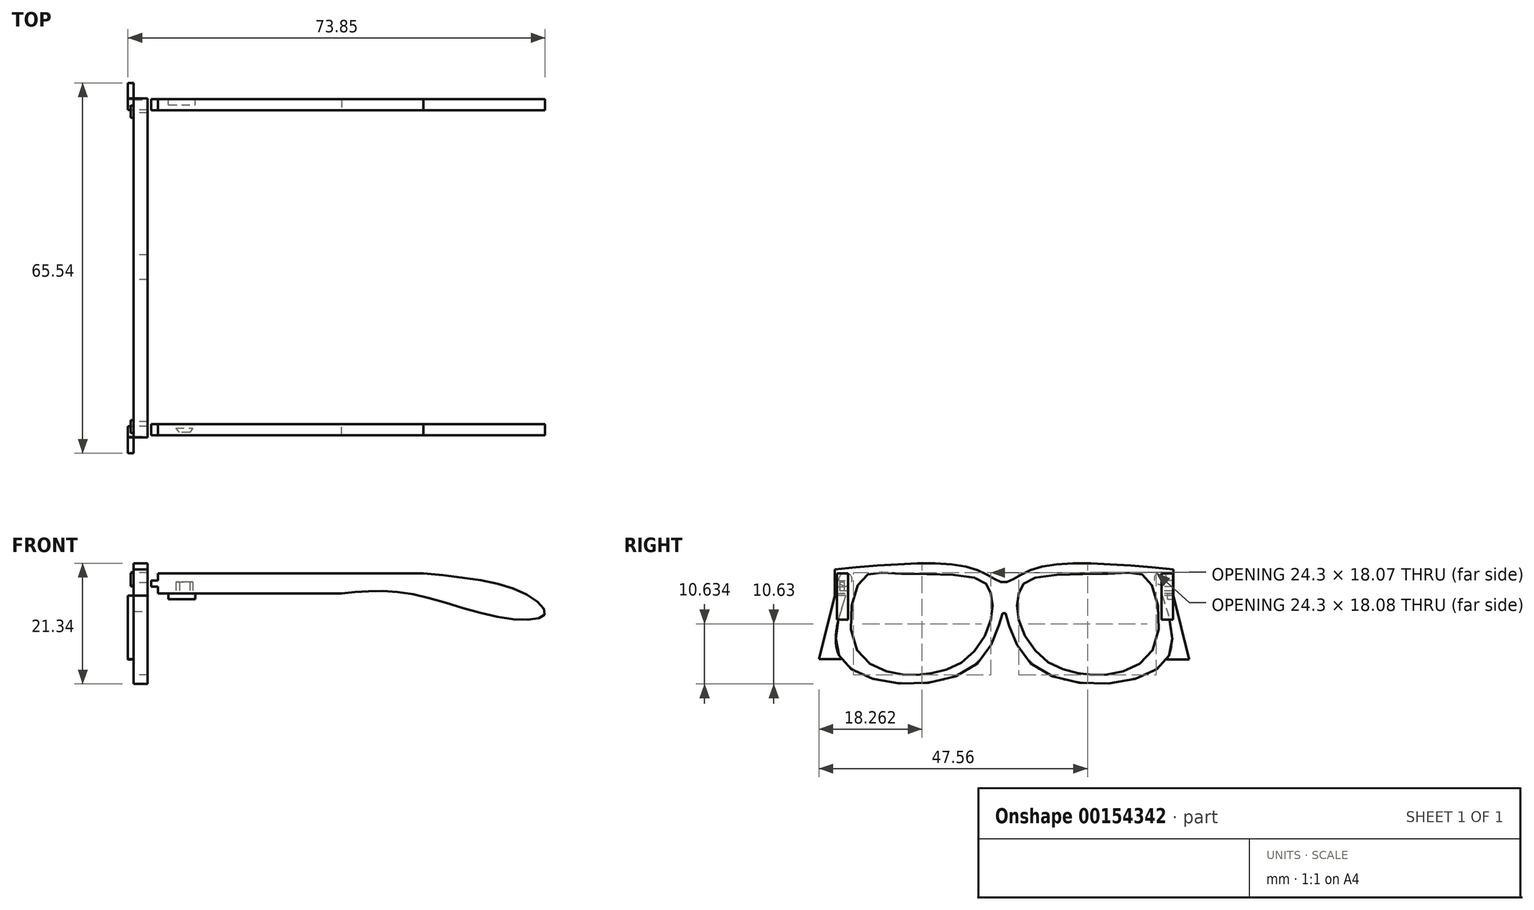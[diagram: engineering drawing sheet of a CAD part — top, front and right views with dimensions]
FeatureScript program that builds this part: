
annotation { "Feature Type Name" : "Feature", "Feature Type Description" : "" }
export const myFeature = defineFeature(function(context is Context, id is Id, definition is map)
    precondition{}
    {
        {
            var Q0;
            Q0=qCreatedBy(makeId("Front.planeOp"),FACE);
            var sketch = newSketch(context, id + "F0", { "sketchPlane" : qUnion([Q0])});
            skLineSegment(sketch, "E0", {"start": v(-30.17, 0) * mm, "end": v(-30.17, 1.2) * mm});
            skLineSegment(sketch, "E1", {"start": v(-30.17, 1.2) * mm, "end": v(-31.35, 1.2) * mm});
            skLineSegment(sketch, "E2", {"start": v(-31.35, 1.2) * mm, "end": v(-31.35, 2.3) * mm});
            skLineSegment(sketch, "E3", {"start": v(-31.35, 2.3) * mm, "end": v(-30.17, 2.3) * mm});
            skLineSegment(sketch, "E4", {"start": v(-30.17, 2.3) * mm, "end": v(-30.17, 3.57) * mm});
            skLineSegment(sketch, "E5", {"start": v(-30.17, 3.57) * mm, "end": v(16.84, 3.57) * mm});
            skLineSegment(sketch, "E6", {"start": v(-30.17, 0) * mm, "end": v(2.32, 0) * mm});
            skFitSpline(sketch, "E7", {"points": [v(16.84, 3.57) * mm, v(34.72, 0) * mm, v(38.32, -3.7) * mm, v(31, -4.33) * mm, v(14.06, 0) * mm, v(2.32, 0) * mm], "startDerivative": vector(80.04, -8.07) * mm, "endDerivative": vector(-54.78, -5.44) * mm});
            skSolve(sketch);
        }
        {
            var Q0;
            Q0=makeQuery(id+"F0.imprint","IMPRINT",FACE,{"disambiguationData":[TD([[makeQuery(id+"F0.imprint","IMPRINT",EDGE,{"derivedFrom":sQuery(id+"F0.wireOp",EDGE,"E0")}),-1.0]])]});
            extrude(context, id + "F1", {"entities" : qUnion([Q0]), "endBound" : BoundingType.SYMMETRIC, "depth" : 2 * mm});
        }
        {
            var Q0;
            Q0=makeQuery(id+"F1.opExtrude","SWEPT_BODY",BODY,{"disambiguationData":[OSD([sQuery(id+"F0.wireOp",EDGE,"E0"),sQuery(id+"F0.wireOp",EDGE,"E1"),sQuery(id+"F0.wireOp",EDGE,"E2"),sQuery(id+"F0.wireOp",EDGE,"E3"),sQuery(id+"F0.wireOp",EDGE,"E4"),sQuery(id+"F0.wireOp",EDGE,"E5"),sQuery(id+"F0.wireOp",EDGE,"E6"),sQuery(id+"F0.wireOp",EDGE,"E7")])]});
            var Q1;
            Q1=makeQuery(id+"F1.opExtrude","CAP_FACE",FACE,{"disambiguationData":[OSD([sQuery(id+"F0.wireOp",EDGE,"E0"),sQuery(id+"F0.wireOp",EDGE,"E1"),sQuery(id+"F0.wireOp",EDGE,"E2"),sQuery(id+"F0.wireOp",EDGE,"E3"),sQuery(id+"F0.wireOp",EDGE,"E4"),sQuery(id+"F0.wireOp",EDGE,"E5"),sQuery(id+"F0.wireOp",EDGE,"E6"),sQuery(id+"F0.wireOp",EDGE,"E7")])],"isStart":false});
            mirror(context, id + "F2", {"entities" : qUnion([Q0]), "mirrorPlane" : qUnion([Q1])});
        }
        {
            var Q0;
            Q0=makeQuery(id+"F2.opPattern","COPY",BODY,{"derivedFrom":makeQuery(id+"F1.opExtrude","SWEPT_BODY",BODY,{"disambiguationData":[OSD([sQuery(id+"F0.wireOp",EDGE,"E0"),sQuery(id+"F0.wireOp",EDGE,"E1"),sQuery(id+"F0.wireOp",EDGE,"E2"),sQuery(id+"F0.wireOp",EDGE,"E3"),sQuery(id+"F0.wireOp",EDGE,"E4"),sQuery(id+"F0.wireOp",EDGE,"E5"),sQuery(id+"F0.wireOp",EDGE,"E6"),sQuery(id+"F0.wireOp",EDGE,"E7")])]}),"instanceName":"1"});
            transform(context, id + "F3", {"entities" : qUnion([Q0]), "transformType" : TransformType.TRANSLATION_3D, "dx" : 0 * mm, "dy" : 50.13 * mm, "dz" : 0 * mm, "makeCopy" : false});
        }
        {
            var Q0;
            Q0=qCreatedBy(makeId("Right.planeOp"),FACE);
            var sketch = newSketch(context, id + "F4", { "sketchPlane" : qUnion([Q0])});
            skLineSegment(sketch, "E8", {"start": v(53.4, 28.28) * mm, "end": v(53.4, 23.62) * mm});
            skLineSegment(sketch, "E9", {"start": v(-6.6, 23.62) * mm, "end": v(-6.6, 28.28) * mm});
            skPoint(sketch, "E10", {"position": v(28.4, 28.28) * mm});
            skPoint(sketch, "E11", {"position": v(18.4, 28.28) * mm});
            skPoint(sketch, "E12.2.internal.snap0", {"position": v(53.4, 25.95) * mm});
            skFitSpline(sketch, "E12", {"points": [v(53.4, 28.28) * mm, v(28.4, 28.28) * mm, v(23.4, 25.95) * mm, v(18.4, 28.28) * mm, v(-6.6, 28.28) * mm], "startDerivative": vector(-87.84, 8.09) * mm, "endDerivative": vector(-87.84, -8.09) * mm});
            skPoint(sketch, "E13", {"position": v(51.4, 23.62) * mm});
            skPoint(sketch, "E14", {"position": v(-4.6, 23.62) * mm});
            skFitSpline(sketch, "E15", {"points": [v(51.4, 23.62) * mm, v(51.4, 11.38) * mm, v(28.4, 11.38) * mm, v(23.4, 20.85) * mm, v(18.4, 11.38) * mm, v(-4.6, 11.38) * mm, v(-4.6, 23.62) * mm], "startDerivative": vector(30.78, -92.04) * mm, "endDerivative": vector(30.78, 92.04) * mm});
            skLineSegment(sketch, "E16", {"start": v(53.4, 23.62) * mm, "end": v(51.4, 23.62) * mm});
            skLineSegment(sketch, "E17", {"start": v(-4.6, 23.62) * mm, "end": v(-6.6, 23.62) * mm});
            skSolve(sketch);
        }
        {
            var Q0;
            Q0=makeQuery(id+"F4.imprint","IMPRINT",FACE,{"disambiguationData":[TD([[makeQuery(id+"F4.imprint","IMPRINT",EDGE,{"derivedFrom":sQuery(id+"F4.wireOp",EDGE,"E8")}),-1.0]])]});
            extrude(context, id + "F5", {"entities" : qUnion([Q0]), "endBound" : BoundingType.SYMMETRIC, "depth" : 2.5 * mm});
        }
        {
            var Q0;
            Q0=makeQuery(id+"F5.opExtrude","SWEPT_BODY",BODY,{"disambiguationData":[OSD([sQuery(id+"F4.wireOp",EDGE,"E8"),sQuery(id+"F4.wireOp",EDGE,"E9"),sQuery(id+"F4.wireOp",EDGE,"E12"),sQuery(id+"F4.wireOp",EDGE,"E15"),sQuery(id+"F4.wireOp",EDGE,"E16"),sQuery(id+"F4.wireOp",EDGE,"E17")])]});
            transform(context, id + "F6", {"entities" : qUnion([Q0]), "transformType" : TransformType.TRANSLATION_3D, "dx" : -33.23 * mm, "dy" : -4.17 * mm, "dz" : -24.03 * mm, "makeCopy" : false});
        }
        {
            var Q0;
            Q0=makeQuery(id+"F1.opExtrude","SWEPT_BODY",BODY,{"disambiguationData":[OSD([sQuery(id+"F0.wireOp",EDGE,"E0"),sQuery(id+"F0.wireOp",EDGE,"E1"),sQuery(id+"F0.wireOp",EDGE,"E2"),sQuery(id+"F0.wireOp",EDGE,"E3"),sQuery(id+"F0.wireOp",EDGE,"E4"),sQuery(id+"F0.wireOp",EDGE,"E5"),sQuery(id+"F0.wireOp",EDGE,"E6"),sQuery(id+"F0.wireOp",EDGE,"E7")])]});
            transform(context, id + "F7", {"entities" : qUnion([Q0]), "transformType" : TransformType.TRANSLATION_3D, "dx" : 0 * mm, "dy" : -9.4 * mm, "dz" : 0 * mm, "makeCopy" : false});
        }
        {
            var Q0;
            Q0=qCreatedBy(makeId("Right.planeOp"),FACE);
            var sketch = newSketch(context, id + "F8", { "sketchPlane" : qUnion([Q0])});
            skPoint(sketch, "E18", {"position": v(19.36, -3.2) * mm});
            skPoint(sketch, "E19", {"position": v(19.23, 1.99) * mm});
            skPoint(sketch, "E20", {"position": v(19.36, 0) * mm});
            skPoint(sketch, "E21", {"position": v(16.86, 0) * mm});
            skPoint(sketch, "E22", {"position": v(21.86, 0) * mm});
            skPoint(sketch, "E23", {"position": v(16.86, -4.94) * mm});
            skPoint(sketch, "E24", {"position": v(21.86, -4.94) * mm});
            skPoint(sketch, "E25", {"position": v(14.86, 0) * mm});
            skPoint(sketch, "E26", {"position": v(23.86, 0) * mm});
            skPoint(sketch, "E27", {"position": v(14.86, 2.49) * mm});
            skPoint(sketch, "E28", {"position": v(23.86, 2.49) * mm});
            skPoint(sketch, "E29", {"position": v(0, 2.49) * mm});
            skPoint(sketch, "E30", {"position": v(38.72, 2.49) * mm});
            skPoint(sketch, "E31", {"position": v(-6, 2.49) * mm});
            skPoint(sketch, "E32", {"position": v(44.72, 2.49) * mm});
            skPoint(sketch, "E33", {"position": v(-7.14, -4.94) * mm});
            skPoint(sketch, "E34", {"position": v(45.86, -4.94) * mm});
            skPoint(sketch, "E35", {"position": v(-7.14, -9.44) * mm});
            skPoint(sketch, "E36", {"position": v(45.86, -9.44) * mm});
            skPoint(sketch, "E37", {"position": v(0, -14.17) * mm});
            skPoint(sketch, "E38", {"position": v(38.72, -14.17) * mm});
            skPoint(sketch, "E39", {"position": v(6, -14.17) * mm});
            skPoint(sketch, "E40", {"position": v(32.72, -14.17) * mm});
            skPoint(sketch, "E41", {"position": v(12.26, -11.85) * mm});
            skPoint(sketch, "E42", {"position": v(12.26, 0) * mm});
            skPoint(sketch, "E43", {"position": v(26.46, 0) * mm});
            skPoint(sketch, "E44", {"position": v(-6, 3.53) * mm});
            skPoint(sketch, "E45", {"position": v(-5.94, 3.53) * mm});
            skPoint(sketch, "E46", {"position": v(0, 3.53) * mm});
            skFitSpline(sketch, "E47", {"points": [v(16.86, -0.02) * mm, v(14.86, 2.49) * mm, v(0, 3.53) * mm, v(-6, 2.49) * mm, v(-7.14, -9.44) * mm, v(0, -14.17) * mm, v(6, -14.17) * mm, v(12.26, -11.85) * mm, v(16.86, -4.94) * mm, v(16.86, -0.02) * mm]});
            skPoint(sketch, "E48", {"position": v(12.26, -11.76) * mm});
            skPoint(sketch, "E49", {"position": v(38.72, 3.53) * mm});
            skPoint(sketch, "E50", {"position": v(26.46, -11.76) * mm});
            skFitSpline(sketch, "E51", {"points": [v(21.86, 0) * mm, v(23.86, 2.49) * mm, v(38.72, 3.53) * mm, v(44.72, 2.49) * mm, v(45.86, -9.44) * mm, v(38.72, -14.17) * mm, v(32.72, -14.17) * mm, v(26.46, -11.76) * mm, v(21.86, -4.94) * mm, v(21.86, 0) * mm]});
            skPoint(sketch, "E52", {"position": v(18.84, -4.06) * mm});
            skPoint(sketch, "E53", {"position": v(19.62, -4.06) * mm});
            skSolve(sketch);
        }
        {
            var Q0;
            Q0=makeQuery(id+"F8.imprint","IMPRINT",FACE,{"disambiguationData":[TD([[makeQuery(id+"F8.imprint","IMPRINT",EDGE,{"derivedFrom":sQuery(id+"F8.wireOp",EDGE,"E47")}),1.0]])]});
            var Q1;
            Q1=makeQuery(id+"F8.imprint","IMPRINT",FACE,{"disambiguationData":[TD([[makeQuery(id+"F8.imprint","IMPRINT",EDGE,{"derivedFrom":sQuery(id+"F8.wireOp",EDGE,"E51")}),-1.0]])]});
            extrude(context, id + "F9", {"entities" : qUnion([Q0, Q1]), "operationType" : NewBodyOperationType.REMOVE, "oppositeDirection" : true, "depth" : 72.6 * mm});
        }
        {
            var Q0;
            Q0=makeQuery(id+"F5.opExtrude","CAP_FACE",FACE,{"disambiguationData":[OSD([sQuery(id+"F4.wireOp",EDGE,"E8"),sQuery(id+"F4.wireOp",EDGE,"E9"),sQuery(id+"F4.wireOp",EDGE,"E12"),sQuery(id+"F4.wireOp",EDGE,"E15"),sQuery(id+"F4.wireOp",EDGE,"E16"),sQuery(id+"F4.wireOp",EDGE,"E17")])],"isStart":true});
            var sketch = newSketch(context, id + "F10", { "sketchPlane" : qUnion([Q0])});
            skLineSegment(sketch, "E54", {"start": v(10.78, -0.41) * mm, "end": v(13.55, -11.67) * mm});
            skLineSegment(sketch, "E55", {"start": v(-49.22, -0.41) * mm, "end": v(-51.99, -11.73) * mm});
            skLineSegment(sketch, "E56", {"start": v(-51.99, -11.73) * mm, "end": v(-48.01, -11.73) * mm});
            skLineSegment(sketch, "E57", {"start": v(9.6, -11.66) * mm, "end": v(-48.06, -11.66) * mm, "construction": true});
            skLineSegment(sketch, "E58", {"start": v(13.55, -11.67) * mm, "end": v(9.6, -11.66) * mm});
            skSolve(sketch);
        }
        {
            var Q0;
            Q0 = qSketchRegion(id + "F10", true);
            var Q1;
            Q1=makeQuery(id+"F10.imprint","IMPRINT",FACE,{"disambiguationData":[TD([[makeQuery(id+"F10.imprint","IMPRINT",EDGE,{"derivedFrom":sQuery(id+"F10.wireOp",EDGE,"E55")}),1.0]])]});
            var Q2;
            Q2=makeQuery(id+"F10.imprint","IMPRINT",FACE,{"disambiguationData":[TD([[makeQuery(id+"F10.imprint","IMPRINT",EDGE,{"derivedFrom":sQuery(id+"F10.wireOp",EDGE,"E54")}),-1.0]])]});
            extrude(context, id + "F11", {"entities" : qUnion([Q0, Q1, Q2]), "depth" : 1 * mm});
        }
        {
            var Q0;
            Q0=makeQuery(id+"F5.opExtrude","CAP_FACE",FACE,{"disambiguationData":[OSD([sQuery(id+"F4.wireOp",EDGE,"E8"),sQuery(id+"F4.wireOp",EDGE,"E9"),sQuery(id+"F4.wireOp",EDGE,"E12"),sQuery(id+"F4.wireOp",EDGE,"E15"),sQuery(id+"F4.wireOp",EDGE,"E16"),sQuery(id+"F4.wireOp",EDGE,"E17")])],"isStart":true});
            var sketch = newSketch(context, id + "F12", { "sketchPlane" : qUnion([Q0])});
            skCircle(sketch, "E59", {"center": v(8.85, 2.45) * mm, "radius": 1.17 * mm});
            skCircle(sketch, "E60", {"center": v(-46.9, 2.66) * mm, "radius": 1.09 * mm});
            skSolve(sketch);
        }
        {
            var Q0;
            Q0 = qSketchRegion(id + "F12", true);
            extrude(context, id + "F13", {"entities" : qUnion([Q0]), "depth" : .5 * mm});
        }
        {
            var Q0;
            Q0=makeQuery(id+"F2.opPattern","COPY",FACE,{"derivedFrom":makeQuery(id+"F1.opExtrude","CAP_FACE",FACE,{"disambiguationData":[OSD([sQuery(id+"F0.wireOp",EDGE,"E0"),sQuery(id+"F0.wireOp",EDGE,"E1"),sQuery(id+"F0.wireOp",EDGE,"E2"),sQuery(id+"F0.wireOp",EDGE,"E3"),sQuery(id+"F0.wireOp",EDGE,"E4"),sQuery(id+"F0.wireOp",EDGE,"E5"),sQuery(id+"F0.wireOp",EDGE,"E6"),sQuery(id+"F0.wireOp",EDGE,"E7")])],"isStart":false}),"instanceName":"1"});
            var sketch = newSketch(context, id + "F14", { "sketchPlane" : qUnion([Q0])});
            skLineSegment(sketch, "E61.bottom", {"start": v(23.58, 3.57) * mm, "end": v(28.3, 3.57) * mm});
            skLineSegment(sketch, "E61.top", {"start": v(23.58, -1.02) * mm, "end": v(28.3, -1.02) * mm});
            skLineSegment(sketch, "E61.left", {"start": v(23.58, 3.57) * mm, "end": v(23.58, -1.02) * mm});
            skLineSegment(sketch, "E61.right", {"start": v(28.3, 3.57) * mm, "end": v(28.3, -1.02) * mm});
            skSolve(sketch);
        }
        {
            var Q0;
            {var subQ0=sQuery(id+"F14.wireOp",EDGE,"E61.top");Q0=makeQuery(id+"F14.imprint","IMPRINT",FACE,{"disambiguationData":[TD([[makeQuery(id+"F14.imprint","IMPRINT",EDGE,{"derivedFrom":subQ0}),1.0]])]});}
            extrude(context, id + "F15", {"entities" : qUnion([Q0]), "operationType" : NewBodyOperationType.ADD, "oppositeDirection" : true, "depth" : 1 * mm});
        }
        {
            var Q0;
            Q0=makeQuery(id+"F1.opExtrude","SWEPT_FACE",FACE,{"disambiguationData":[OSD([sQuery(id+"F0.wireOp",EDGE,"E6")])]});
            var sketch = newSketch(context, id + "F16", { "sketchPlane" : qUnion([Q0])});
            skLineSegment(sketch, "E62", {"start": v(-26.37, 9.9) * mm, "end": v(-27.01, 9.11) * mm});
            skLineSegment(sketch, "E63", {"start": v(-27.01, 9.11) * mm, "end": v(-24.03, 9.11) * mm});
            skLineSegment(sketch, "E64", {"start": v(-24.03, 9.11) * mm, "end": v(-24.5, 9.85) * mm});
            skLineSegment(sketch, "E65", {"start": v(-24.5, 9.85) * mm, "end": v(-26.37, 9.9) * mm});
            skSolve(sketch);
        }
        {
            var Q0;
            Q0 = qSketchRegion(id + "F16", true);
            extrude(context, id + "F17", {"entities" : qUnion([Q0]), "operationType" : NewBodyOperationType.REMOVE, "oppositeDirection" : true, "depth" : 2 * mm});
        }
    });
